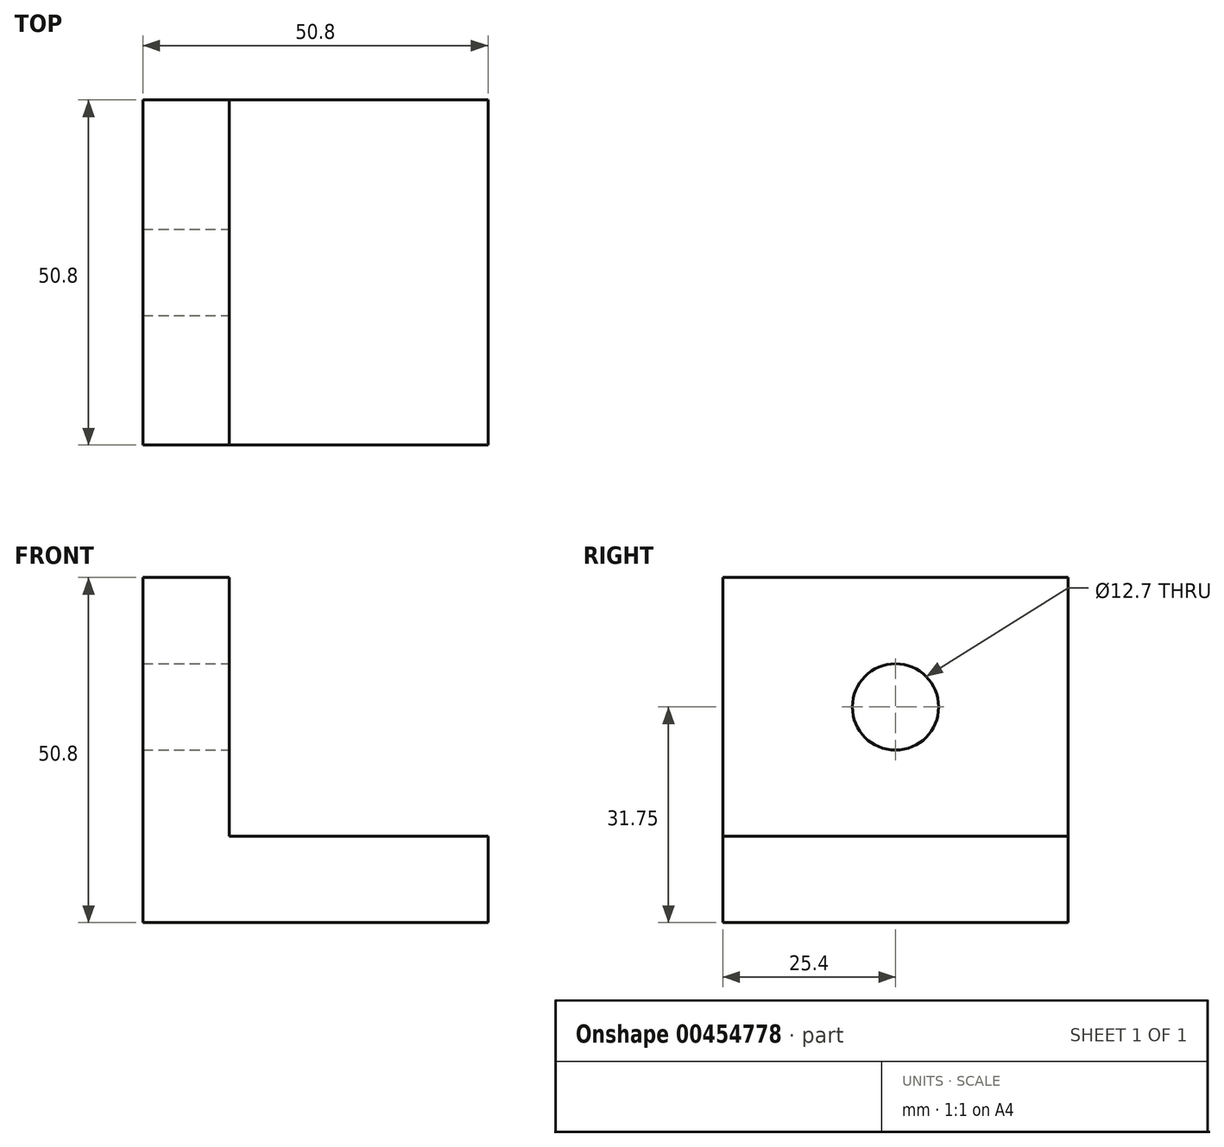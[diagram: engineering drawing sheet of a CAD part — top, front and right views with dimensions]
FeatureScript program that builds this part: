
annotation { "Feature Type Name" : "Feature", "Feature Type Description" : "" }
export const myFeature = defineFeature(function(context is Context, id is Id, definition is map)
    precondition{}
    {
        {
            var Q0;
            Q0=qCreatedBy(makeId("Top.planeOp"),FACE);
            var sketch = newSketch(context, id + "F0", { "sketchPlane" : qUnion([Q0])});
            skLineSegment(sketch, "E0.bottom", {"start": v(3.84, 0) * mm, "end": v(54.64, 0) * mm});
            skLineSegment(sketch, "E0.top", {"start": v(3.84, 50.8) * mm, "end": v(54.64, 50.8) * mm});
            skLineSegment(sketch, "E0.left", {"start": v(3.84, 0) * mm, "end": v(3.84, 50.8) * mm});
            skLineSegment(sketch, "E0.right", {"start": v(54.64, 0) * mm, "end": v(54.64, 50.8) * mm});
            skSolve(sketch);
        }
        {
            var Q0;
            Q0 = qSketchRegion(id + "F0", true);
            extrude(context, id + "F1", {"entities" : qUnion([Q0]), "depth" : 12.7 * mm});
        }
        {
            var Q0;
            Q0=makeQuery(id+"F1.opExtrude","CAP_FACE",FACE,{"disambiguationData":[OSD([sQuery(id+"F0.wireOp",EDGE,"E0.bottom"),sQuery(id+"F0.wireOp",EDGE,"E0.top"),sQuery(id+"F0.wireOp",EDGE,"E0.left"),sQuery(id+"F0.wireOp",EDGE,"E0.right")])],"isStart":false});
            var sketch = newSketch(context, id + "F2", { "sketchPlane" : qUnion([Q0])});
            skLineSegment(sketch, "E1.bottom", {"start": v(3.84, 0) * mm, "end": v(16.54, 0) * mm});
            skLineSegment(sketch, "E1.top", {"start": v(3.84, 50.8) * mm, "end": v(16.54, 50.8) * mm});
            skLineSegment(sketch, "E1.left", {"start": v(3.84, 0) * mm, "end": v(3.84, 50.8) * mm});
            skLineSegment(sketch, "E1.right", {"start": v(16.54, 0) * mm, "end": v(16.54, 50.8) * mm});
            skSolve(sketch);
        }
        {
            var Q0;
            Q0 = qSketchRegion(id + "F2", true);
            extrude(context, id + "F3", {"entities" : qUnion([Q0]), "operationType" : NewBodyOperationType.ADD, "depth" : 38.1 * mm});
        }
        {
            var Q0;
            Q0=makeQuery(id+"F3.opExtrude","SWEPT_FACE",FACE,{"disambiguationData":[OSD([sQuery(id+"F2.wireOp",EDGE,"E1.right")])]});
            var sketch = newSketch(context, id + "F4", { "sketchPlane" : qUnion([Q0])});
            skCircle(sketch, "E2", {"center": v(25.4, 31.75) * mm, "radius": 6.35 * mm});
            skSolve(sketch);
        }
        {
            var Q0;
            Q0 = qSketchRegion(id + "F4", true);
            extrude(context, id + "F5", {"entities" : qUnion([Q0]), "operationType" : NewBodyOperationType.REMOVE, "oppositeDirection" : true, "depth" : 25.4 * mm});
        }
    });
